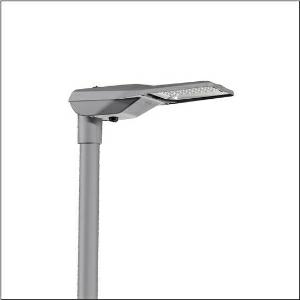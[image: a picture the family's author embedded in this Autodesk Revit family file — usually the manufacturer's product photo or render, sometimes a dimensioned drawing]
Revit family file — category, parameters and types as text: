
# Revit family: streetlight_sl_21_mini___pl52_5xe2h43t08gb_d0a8
name_source: partatom
category: Lighting Fixtures
units: mm (PartAtom-declared; Revit-internal decimal feet)

## family parameters
Cut with Voids When Loaded = No
Host = Face
Light Source = No
Part Type = Normal
Room Calculation Point = No
Round Connector Dimension = Use Diameter
Shared = No

## types (1)
- --- (1 x LED, 6080 lm, 40.4 W, 4000K)
    Apparent Load = 40 VA
    CIE Flux Codes = 27 59 98 100 100
    Color Rendering = 70
    Color Temperature = 4000K
    Default Elevation = 1800 mm
    Description = Streetlight SL 21 mini, mast luminaire, primary light control with lens, of PMMA, primary optical cover: cover, of toughened safety glass, transparent, light distribution: PL52, light emission: direct distribution, primary light characteristic: asymmetric, installation type: side-entry, post-top, LED, High Power LED, rated luminous flux: 6.080lm, luminous efficacy: 151lm/W, light colour: 740, colour temperature: 4000K, control gear: D4i, control: overheat protection, constant luminous flux control, time-dependent luminous flux control, flexible luminous flux parameterisation, pre-setting: logarithmic dimming characteristic, mains connection: 220..240V, AC, 50/60Hz, start of lifetime: 40W, end of service life: 41W, reduction: 19W, luminaire housing, of diecast aluminium, powder-coated, SITECO metallic grey (DB 702S), corrosivity category C5 high according to DIN EN ISO 12944, please order mast flange separately, inclination adjustable: 0°, 5°, 10°, 15°, sealing non-destructively replaceable, multi-level sealing system, length: 628mm, width: 235mm, height: 110mm, mast flange for spigot size: 42mm (side-entry): 5XC10008XM4, 60/48mm (side-entry/post-top): 5XC10108XM2, 76/60mm (side-entry/post-top): 5XC10108XM1, mounting height: 4..8m, Smart Interface below and above, protection rating (complete): IP66, insulation class (complete): insulation class II (safety insulation), certification: CE, ENEC, ENEC+, VDE, impact resistance: IK10, permissible operating ambient temperature for outdoor applications: -40..+50°C, standard-compliant lighting for roads and squares, packaging unit: 1 piece

Light Distribution: PL52
    Height = 110 mm
    Lamp = 1 x LED
    Lamp Light Flux = 6080 lm
    Lamp Power = 40.4 W
    Lamp count = 1
    Length = 625 mm
    Luminous efficacy = 151 lm/W
    Manufacturer = Siteco
    ModVariant = No
    Model = 5XE2H43T08GB
    Number of Poles = 1
    OnlyDefault = Yes
    Power Factor = 1
    Product Name = Streetlight SL 21 mini | PL52
    Product group = mast luminaire | pylon top
    ProductGroupID = 6100
    Protection Class = Protection class II
    Protection Degree = IP 66
    RLX_Detail_Level = 1
    RLX_Emergency_Light_Flux = 0 lm
    RLX_Emergency_Type = 0
    RLX_Emergency_Type_DB = No
    RlxData = <blob elided: 35965 chars, md5=892bf797>
    Socket = socket
    Standby Power = 0 W
    System Light Flux = 6080 lm
    System Power = 40 W
    Type Comments = factory setting: luminous flux: 100 % | dim-lin: 254 | 812 mA
    Type Image = l_1003514.jpg
    URL = http://relux.com
    VarID = @adj_187483
    Voltage = 0 V
    Weight = 0.00 kg
    Width = 234 mm

## geometry (parser evidence)
native form markers: Blend x4, Sweep x11
no freeform markers — native parametric forms only
